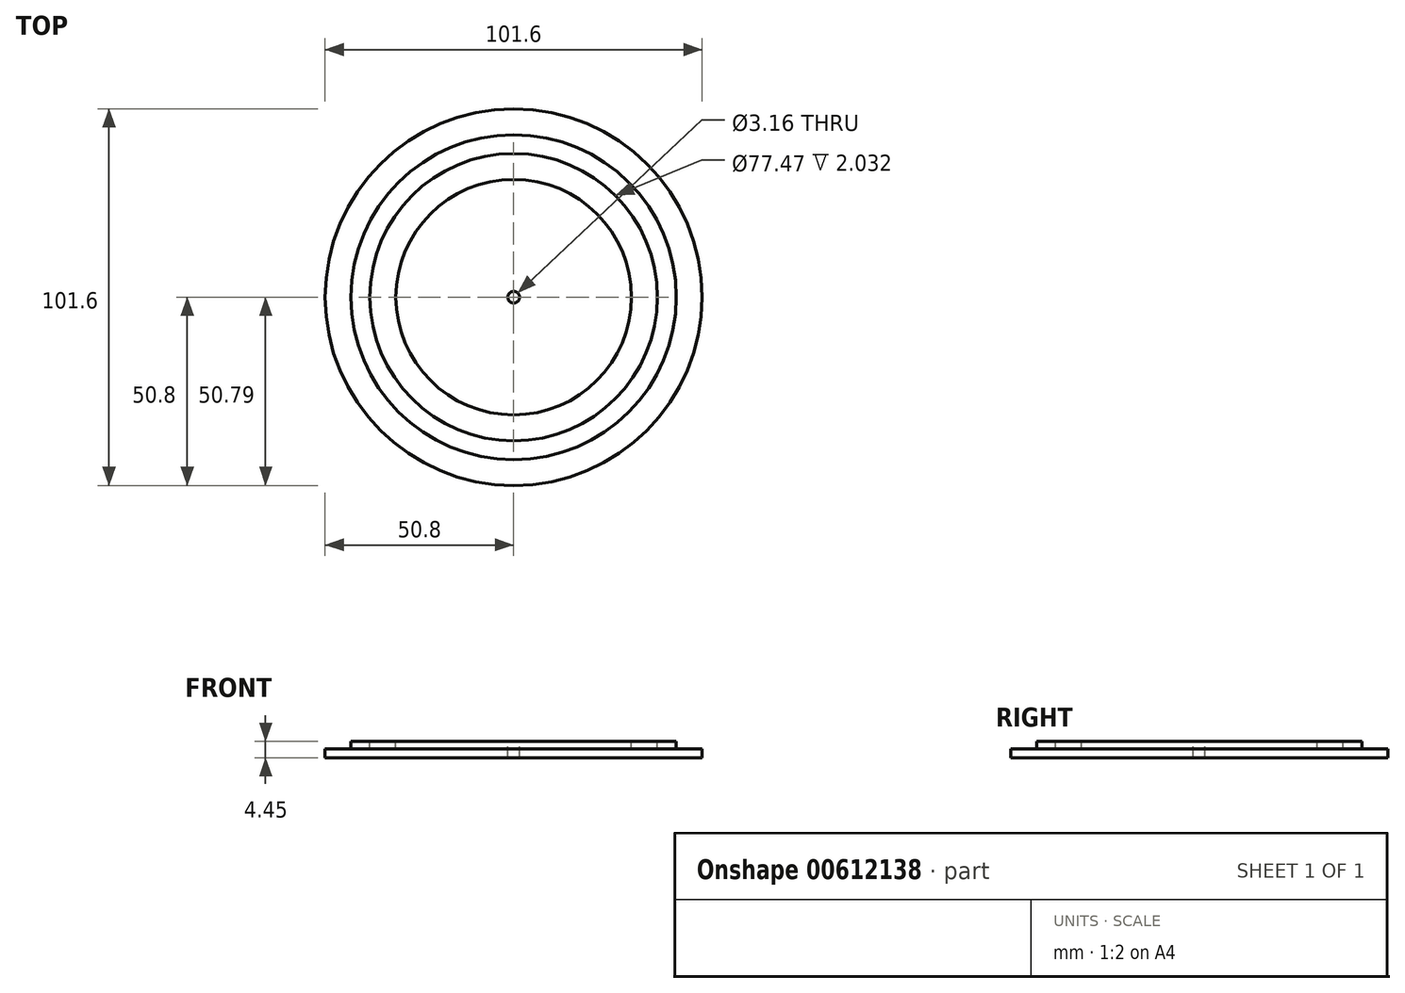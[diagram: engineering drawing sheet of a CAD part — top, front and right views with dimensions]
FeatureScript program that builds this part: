
annotation { "Feature Type Name" : "Feature", "Feature Type Description" : "" }
export const myFeature = defineFeature(function(context is Context, id is Id, definition is map)
    precondition{}
    {
        {
            var Q0;
            Q0=qCreatedBy(makeId("Top.planeOp"),FACE);
            var sketch = newSketch(context, id + "F0", { "sketchPlane" : qUnion([Q0])});
            skCircle(sketch, "E0", {"center": v(0, 0) * mm, "radius": 50.8 * mm});
            skCircle(sketch, "E1", {"center": v(0, 0) * mm, "radius": 43.82 * mm});
            skCircle(sketch, "E2", {"center": v(0, 0) * mm, "radius": 38.73 * mm});
            skCircle(sketch, "E3", {"center": v(0, 0) * mm, "radius": 31.75 * mm});
            skCircle(sketch, "E4", {"center": v(0, 0) * mm, "radius": 1.58 * mm});
            skSolve(sketch);
        }
        {
            var Q0;
            Q0=makeQuery(id+"F0.imprint","IMPRINT",FACE,{"disambiguationData":[TD([[makeQuery(id+"F0.imprint","IMPRINT",EDGE,{"derivedFrom":sQuery(id+"F0.wireOp",EDGE,"E0")}),1.0]])]});
            var Q1;
            Q1=makeQuery(id+"F0.imprint","IMPRINT",FACE,{"disambiguationData":[TD([[makeQuery(id+"F0.imprint","IMPRINT",EDGE,{"derivedFrom":sQuery(id+"F0.wireOp",EDGE,"E3")}),1.0]])]});
            var Q2;
            Q2=makeQuery(id+"F0.imprint","IMPRINT",FACE,{"disambiguationData":[TD([[makeQuery(id+"F0.imprint","IMPRINT",EDGE,{"derivedFrom":sQuery(id+"F0.wireOp",EDGE,"E1")}),1.0]])]});
            var Q3;
            Q3=makeQuery(id+"F0.imprint","IMPRINT",FACE,{"disambiguationData":[TD([[makeQuery(id+"F0.imprint","IMPRINT",EDGE,{"derivedFrom":sQuery(id+"F0.wireOp",EDGE,"E2")}),1.0]])]});
            extrude(context, id + "F1", {"entities" : qUnion([Q0, Q1, Q2, Q3]), "oppositeDirection" : true, "depth" : 4.44 * mm, "offsetDistance" : 25.4 * mm});
        }
        {
            var Q0;
            Q0=makeQuery(id+"F0.imprint","IMPRINT",FACE,{"disambiguationData":[TD([[makeQuery(id+"F0.imprint","IMPRINT",EDGE,{"derivedFrom":sQuery(id+"F0.wireOp",EDGE,"E0")}),1.0]])]});
            var Q1;
            Q1=makeQuery(id+"F0.imprint","IMPRINT",FACE,{"disambiguationData":[TD([[makeQuery(id+"F0.imprint","IMPRINT",EDGE,{"derivedFrom":sQuery(id+"F0.wireOp",EDGE,"E2")}),1.0]])]});
            extrude(context, id + "F2", {"entities" : qUnion([Q0, Q1]), "operationType" : NewBodyOperationType.REMOVE, "oppositeDirection" : true, "depth" : 2.03 * mm, "offsetDistance" : 25.4 * mm});
        }
    });
